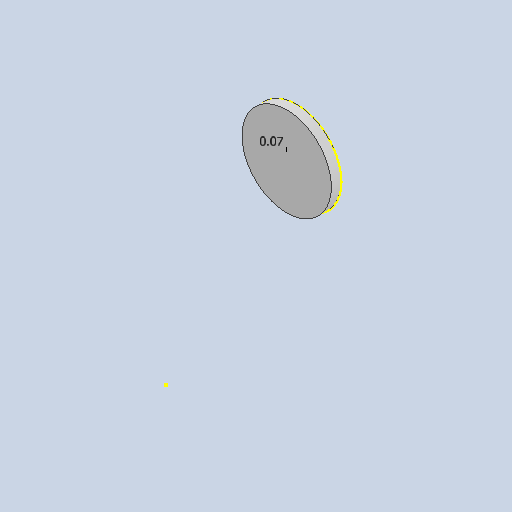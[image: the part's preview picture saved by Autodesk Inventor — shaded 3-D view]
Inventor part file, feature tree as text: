
AUTODESK INVENTOR PART (.ipt)
format: ipt  version: 2023 (Build 270158000, 158)  size: 242,176 bytes
history: native  units: mm
features: other x4, extrude x2, reference x2, plane x1, sketch x1
ambient origin geometry x8: Origin, YZ Plane, XZ Plane, XY Plane, X Axis, Y Axis, Z Axis, Center Point
bodies: Solid1 (feature_tree)
feature tree (10):
  plane  "Work Plane1"
  sketch  "Sketch1"  dims[d0=0.07mm d1=2.0mm d2=0.0mm d3=3.0mm d4=0.0mm]
  extrude  "Extrusion1"  Depth=2.0mm TaperAngle=0.0deg
  extrude  "Extrusion2"  Depth=3.0mm TaperAngle=0.0deg
  reference  "Reference1"
  reference  "Reference2"
  parser-record x1  (decoder bookkeeping rows leaked as tree rows — omitted from the tree; the rows remain in map.json)
  other  "doorLockAssembly_V3.iam"
  other  "pin_V3:1"
  other  "spacerB_V3:1"
note: 1 file-system path scrubbed to <path> (originals preserved in map.json)
